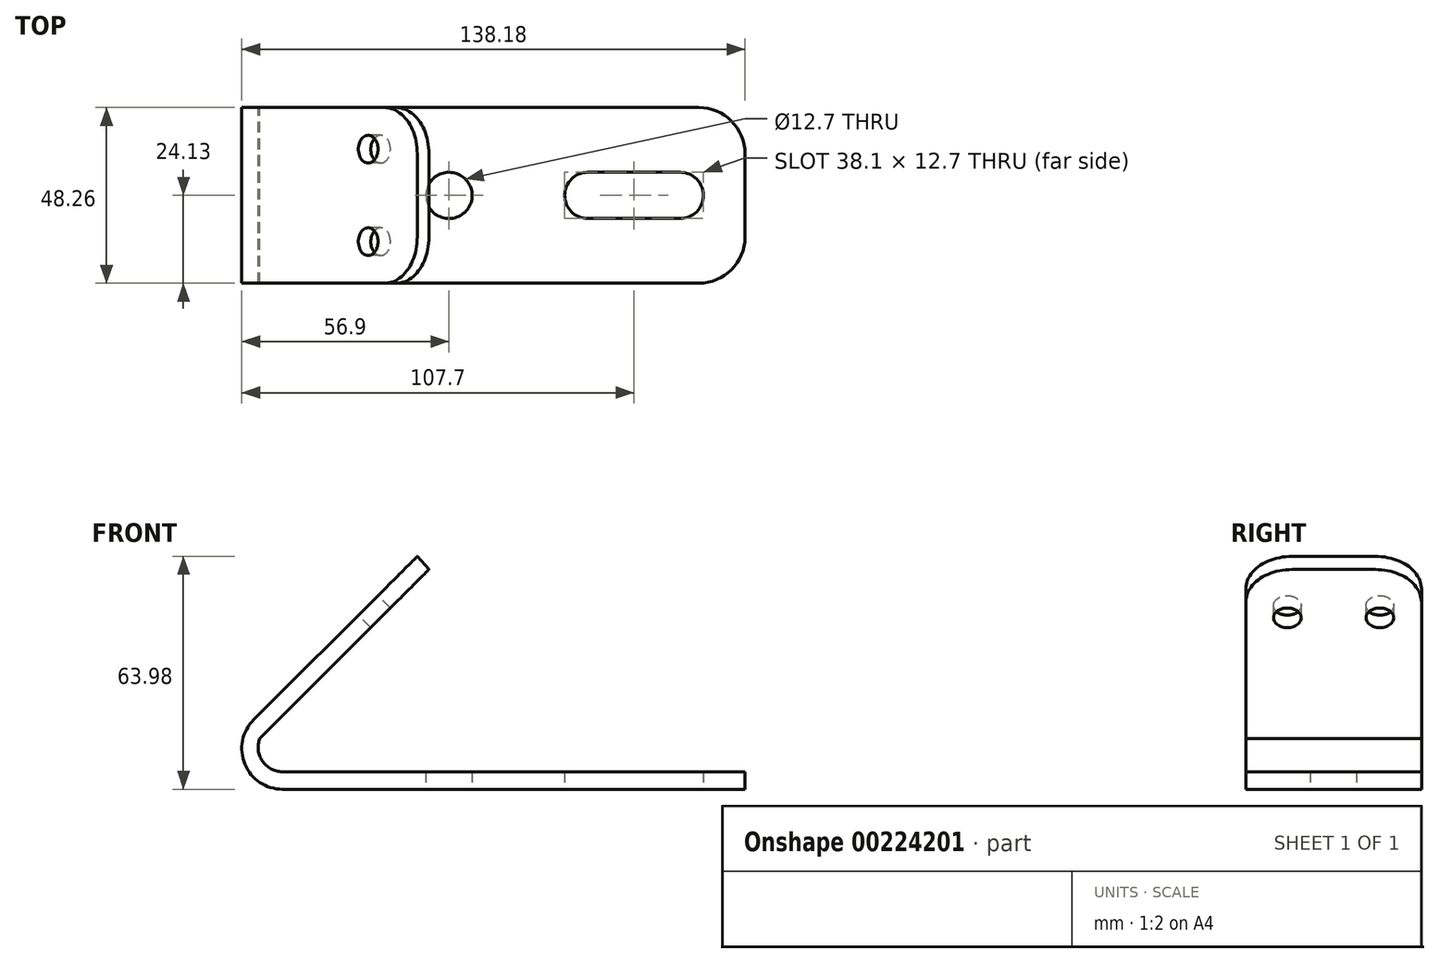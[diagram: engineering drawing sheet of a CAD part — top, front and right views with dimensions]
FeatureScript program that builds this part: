
annotation { "Feature Type Name" : "Feature", "Feature Type Description" : "" }
export const myFeature = defineFeature(function(context is Context, id is Id, definition is map)
    precondition{}
    {
        {
            var Q0;
            Q0=qCreatedBy(makeId("Top.planeOp"),FACE);
            var sketch = newSketch(context, id + "F0", { "sketchPlane" : qUnion([Q0])});
            skLineSegment(sketch, "E0.bottom", {"start": v(50.8, 24.13) * mm, "end": v(-63.5, 24.13) * mm});
            skLineSegment(sketch, "E0.top", {"start": v(50.8, -24.13) * mm, "end": v(-63.5, -24.13) * mm});
            skLineSegment(sketch, "E0.left", {"start": v(63.5, 11.43) * mm, "end": v(63.5, -11.43) * mm});
            skLineSegment(sketch, "E0.right", {"start": v(-63.5, 24.13) * mm, "end": v(-63.5, -24.13) * mm});
            skPoint(sketch, "E0.middle", {"position": v(0, 0) * mm});
            skCircle(sketch, "E1", {"center": v(-17.78, 0) * mm, "radius": 6.35 * mm});
            skLineSegment(sketch, "E2.bottom", {"start": v(45.72, 6.35) * mm, "end": v(20.32, 6.35) * mm});
            skLineSegment(sketch, "E2.top", {"start": v(45.72, -6.35) * mm, "end": v(20.32, -6.35) * mm});
            skPoint(sketch, "E2.middle", {"position": v(33.02, 0) * mm});
            skArc(sketch, "E3", {"start": v(20.32, 6.35) * mm, "mid": v(13.97, 0) * mm, "end": v(20.32, -6.35) * mm});
            skArc(sketch, "E4", {"start": v(45.72, -6.35) * mm, "mid": v(52.07, 0) * mm, "end": v(45.72, 6.35) * mm});
            skLineSegment(sketch, "E5", {"start": v(-63.5, 0) * mm, "end": v(63.5, 0) * mm, "construction": true});
            skPoint(sketch, "E6.visualSharp", {"position": v(63.5, 24.13) * mm});
            skArc(sketch, "E6.filletArc", {"start": v(63.5, 11.43) * mm, "mid": v(59.78, 20.41) * mm, "end": v(50.8, 24.13) * mm});
            skPoint(sketch, "E7.visualSharp", {"position": v(63.5, -24.13) * mm});
            skArc(sketch, "E7.filletArc", {"start": v(50.8, -24.13) * mm, "mid": v(59.78, -20.41) * mm, "end": v(63.5, -11.43) * mm});
            skSolve(sketch);
        }
        {
            var Q0;
            Q0=makeQuery(id+"F0.imprint","IMPRINT",FACE,{"disambiguationData":[TD([[makeQuery(id+"F0.imprint","IMPRINT",EDGE,{"derivedFrom":sQuery(id+"F0.wireOp",EDGE,"E0.bottom")}),1.0]])]});
            extrude(context, id + "F1", {"entities" : qUnion([Q0]), "depth" : 4.83 * mm});
        }
        {
            var Q0;
            Q0=qCreatedBy(makeId("Front.planeOp"),FACE);
            var sketch = newSketch(context, id + "F2", { "sketchPlane" : qUnion([Q0])});
            skLineSegment(sketch, "E8.0", {"start": v(50.8, 4.83) * mm, "end": v(-63.5, 4.83) * mm});
            skLineSegment(sketch, "E9.0", {"start": v(50.8, 0) * mm, "end": v(-63.5, 0) * mm});
            skArc(sketch, "E10", {"start": v(-71.4, 19.08) * mm, "mid": v(-73.83, 6.9) * mm, "end": v(-63.5, 0) * mm});
            skLineSegment(sketch, "E11", {"start": v(-63.5, 4.83) * mm, "end": v(-63.5, 0) * mm});
            skLineSegment(sketch, "E12", {"start": v(-71.4, 19.08) * mm, "end": v(-26.5, 63.98) * mm});
            skArc(sketch, "E13", {"start": v(-69.72, 13.95) * mm, "mid": v(-69.02, 7.74) * mm, "end": v(-63.5, 4.83) * mm});
            skLineSegment(sketch, "E14", {"start": v(-69.72, 13.95) * mm, "end": v(-23.3, 60.38) * mm});
            skLineSegment(sketch, "E15", {"start": v(-23.3, 60.38) * mm, "end": v(-26.5, 63.98) * mm});
            skSolve(sketch);
        }
        {
            var Q0;
            Q0=makeQuery(id+"F2.imprint","IMPRINT",FACE,{"disambiguationData":[TD([[makeQuery(id+"F2.imprint","IMPRINT",EDGE,{"derivedFrom":sQuery(id+"F2.wireOp",EDGE,"E10")}),1.0]])]});
            extrude(context, id + "F3", {"entities" : qUnion([Q0]), "operationType" : NewBodyOperationType.ADD, "endBound" : BoundingType.SYMMETRIC, "depth" : 48.26 * mm});
        }
        {
            var Q0;
            Q0=makeQuery(id+"F3.opExtrude","CAP_EDGE",EDGE,{"disambiguationData":[OSD([sQuery(id+"F2.wireOp",EDGE,"E15")])],"isStart":true});
            fillet(context, id + "F4", {"entities" : qUnion([Q0]), "radius" : 12.7 * mm, "tangentPropagation" : true, "allowEdgeOverflow" : false});
        }
        {
            var Q0;
            Q0=makeQuery(id+"F3.opExtrude","CAP_EDGE",EDGE,{"disambiguationData":[OSD([sQuery(id+"F2.wireOp",EDGE,"E15")])],"isStart":false});
            fillet(context, id + "F5", {"entities" : qUnion([Q0]), "radius" : 12.7 * mm, "tangentPropagation" : true, "allowEdgeOverflow" : false});
        }
        {
            var Q0;
            Q0=makeQuery(id+"F3.opExtrude","SWEPT_FACE",FACE,{"disambiguationData":[OSD([sQuery(id+"F2.wireOp",EDGE,"E12")])]});
            var sketch = newSketch(context, id + "F6", { "sketchPlane" : qUnion([Q0])});
            skLineSegment(sketch, "E16.0", {"start": v(-24.13, -37) * mm, "end": v(-24.13, 13.78) * mm});
            skLineSegment(sketch, "E17.0", {"start": v(24.13, -37) * mm, "end": v(24.13, 13.78) * mm});
            skLineSegment(sketch, "E18.0", {"start": v(24.13, -37) * mm, "end": v(-24.13, -37) * mm});
            skLineSegment(sketch, "E19", {"start": v(24.13, -48.17) * mm, "end": v(-24.13, -48.17) * mm});
            skLineSegment(sketch, "E20.0", {"start": v(11.43, 26.5) * mm, "end": v(-11.43, 26.5) * mm});
            skCircle(sketch, "E21", {"center": v(-12.7, 7.45) * mm, "radius": 3.81 * mm});
            skCircle(sketch, "E22", {"center": v(12.7, 7.45) * mm, "radius": 3.81 * mm});
            skSolve(sketch);
        }
        {
            var Q0;
            Q0=makeQuery(id+"F6.imprint","IMPRINT",FACE,{"disambiguationData":[TD([[makeQuery(id+"F6.imprint","IMPRINT",EDGE,{"derivedFrom":sQuery(id+"F6.wireOp",EDGE,"E21")}),1.0]])]});
            var Q1;
            Q1=makeQuery(id+"F6.imprint","IMPRINT",FACE,{"disambiguationData":[TD([[makeQuery(id+"F6.imprint","IMPRINT",EDGE,{"derivedFrom":sQuery(id+"F6.wireOp",EDGE,"E22")}),1.0]])]});
            extrude(context, id + "F7", {"entities" : qUnion([Q0, Q1]), "operationType" : NewBodyOperationType.REMOVE, "oppositeDirection" : true, "depth" : 25.4 * mm});
        }
    });
